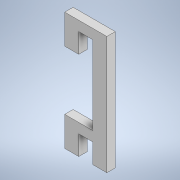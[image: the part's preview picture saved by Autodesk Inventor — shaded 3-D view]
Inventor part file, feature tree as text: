
AUTODESK INVENTOR PART (.ipt)
format: ipt  version: 2020.2 (Build 242310000, 310)  size: 123,392 bytes
history: native  units: in
note: dims shown in document units (in); Inventor stores cm internally (conversion verified against a paired STEP export)
features: extrude x1, sketch x1
ambient origin geometry x8: Origin, YZ Plane, XZ Plane, XY Plane, X Axis, Y Axis, Z Axis, Center Point
bodies: Solid1 (feature_tree)
feature tree (2):
  extrude  "Extrusion1"  Depth=0.175in
  sketch  "Sketch1"  dims[d1=1.4in d2=0.175in d3=0.175in d4=0.25in d6=0.25in d7=0.25in d11=0.15in d12=0.0in d13=0.525in d14=0.525in]
